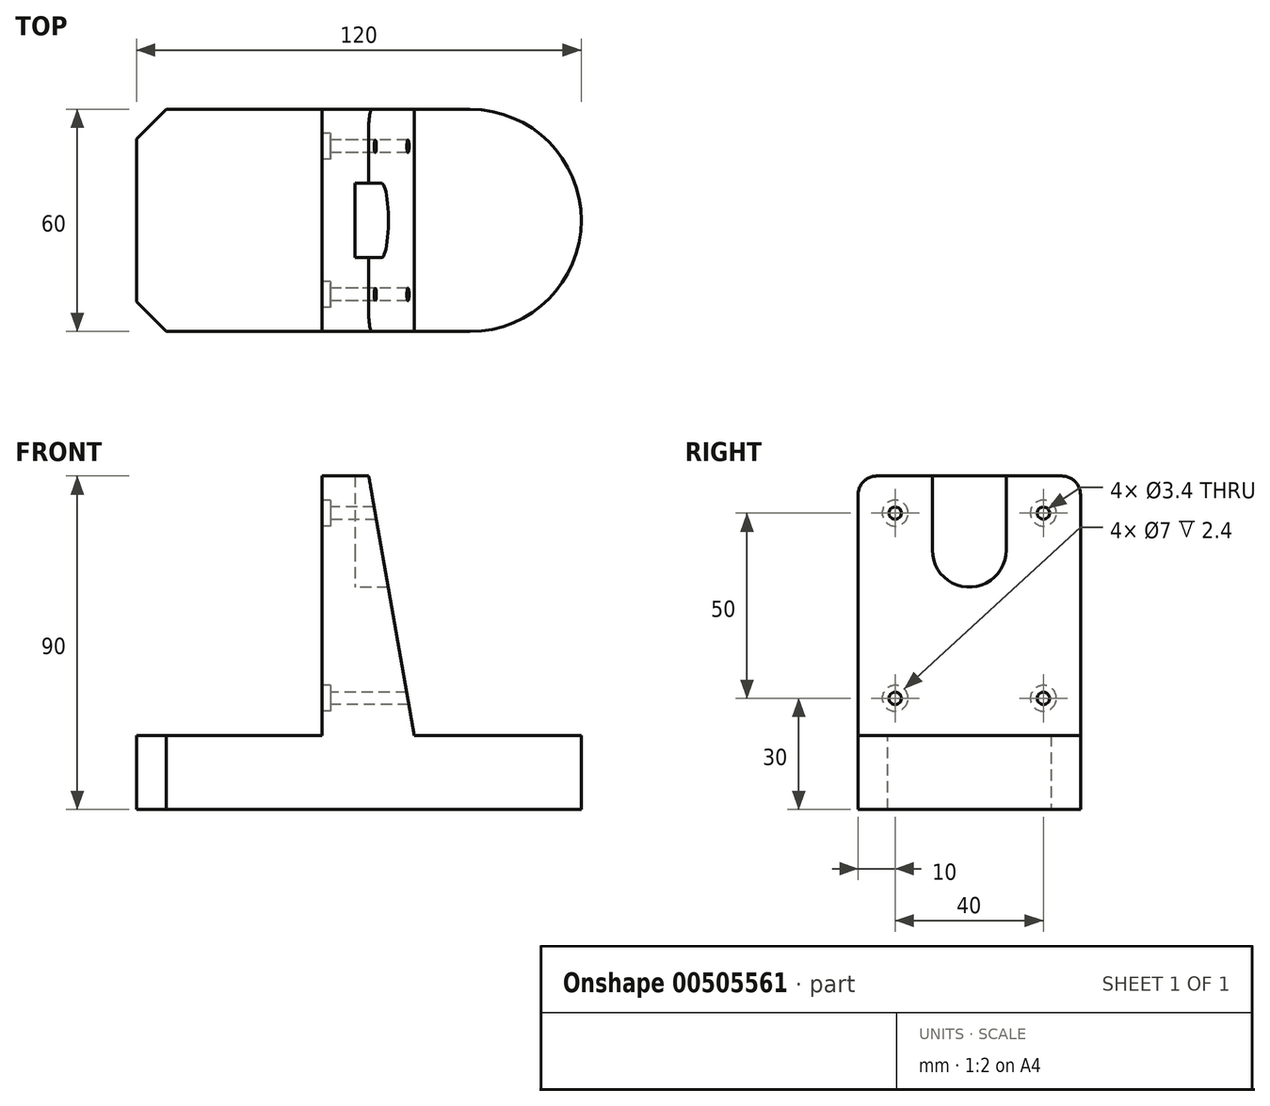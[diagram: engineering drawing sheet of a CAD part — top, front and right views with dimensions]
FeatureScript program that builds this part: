
annotation { "Feature Type Name" : "Feature", "Feature Type Description" : "" }
export const myFeature = defineFeature(function(context is Context, id is Id, definition is map)
    precondition{}
    {
        {
            var Q0;
            Q0=qCreatedBy(makeId("Top.planeOp"),FACE);
            var sketch = newSketch(context, id + "F0", { "sketchPlane" : qUnion([Q0])});
            skLineSegment(sketch, "E0.bottom", {"start": v(0, 0) * mm, "end": v(90, 0) * mm});
            skLineSegment(sketch, "E0.top", {"start": v(0, 60) * mm, "end": v(90, 60) * mm});
            skLineSegment(sketch, "E0.left", {"start": v(0, 0) * mm, "end": v(0, 60) * mm});
            skLineSegment(sketch, "E0.right", {"start": v(90, 0) * mm, "end": v(90, 60) * mm});
            skArc(sketch, "E1", {"start": v(90, 0) * mm, "mid": v(120, 30) * mm, "end": v(90, 60) * mm});
            skSolve(sketch);
        }
        {
            var Q0;
            Q0=qSketchRegion(id+"F0",true);
            extrude(context, id + "F1", {"entities" : qUnion([Q0]), "depth" : 20 * mm});
        }
        {
            var Q0;
            Q0=makeQuery(id+"F1.opExtrude","SWEPT_EDGE",EDGE,{"disambiguationData":[OSD([sQuery(id+"F0.wireOp",EDGE,"E0.bottom"),sQuery(id+"F0.wireOp",EDGE,"E0.left")])]});
            var Q1;
            Q1=makeQuery(id+"F1.opExtrude","SWEPT_EDGE",EDGE,{"disambiguationData":[OSD([sQuery(id+"F0.wireOp",EDGE,"E0.top"),sQuery(id+"F0.wireOp",EDGE,"E0.left")])]});
            chamfer(context, id + "F2", {"entities" : qUnion([Q0, Q1]), "width" : 8 * mm, "tangentPropagation" : true});
        }
        {
            var Q0;
            Q0=qCreatedBy(makeId("Front.planeOp"),FACE);
            var sketch = newSketch(context, id + "F3", { "sketchPlane" : qUnion([Q0])});
            skLineSegment(sketch, "E2", {"start": v(50, 20) * mm, "end": v(75, 20) * mm});
            skLineSegment(sketch, "E3", {"start": v(75, 20) * mm, "end": v(62.66, 90) * mm});
            skLineSegment(sketch, "E4", {"start": v(62.66, 90) * mm, "end": v(50, 90) * mm});
            skLineSegment(sketch, "E5", {"start": v(50, 90) * mm, "end": v(50, 20) * mm});
            skSolve(sketch);
        }
        {
            var Q0;
            Q0=qSketchRegion(id+"F3",true);
            var Q1;
            Q1=makeQuery(id+"F1.opExtrude","SWEPT_FACE",FACE,{"disambiguationData":[OSD([sQuery(id+"F0.wireOp",EDGE,"E0.top")])]});
            extrude(context, id + "F4", {"entities" : qUnion([Q0]), "operationType" : NewBodyOperationType.ADD, "endBound" : BoundingType.UP_TO_SURFACE, "oppositeDirection" : true, "endBoundEntityFace" : qUnion([Q1]), "depth" : 25 * mm});
        }
        {
            var Q0;
            Q0=makeQuery(id+"F4.opExtrude","CAP_EDGE",EDGE,{"disambiguationData":[OSD([sQuery(id+"F3.wireOp",EDGE,"E4")])],"isStart":true});
            var Q1;
            Q1=makeQuery(id+"F4.opExtrude","CAP_EDGE",EDGE,{"disambiguationData":[OSD([sQuery(id+"F3.wireOp",EDGE,"E4")])],"isStart":false});
            fillet(context, id + "F5", {"entities" : qUnion([Q0, Q1]), "radius" : 5 * mm, "tangentPropagation" : true, "allowEdgeOverflow" : false});
        }
        {
            var Q0;
            Q0=makeQuery(id+"F4.opExtrude","SWEPT_FACE",FACE,{"disambiguationData":[OSD([sQuery(id+"F3.wireOp",EDGE,"E5")])]});
            var sketch = newSketch(context, id + "F6", { "sketchPlane" : qUnion([Q0])});
            skLineSegment(sketch, "E6.bottom", {"start": v(-50, 30) * mm, "end": v(-10, 30) * mm, "construction": true});
            skLineSegment(sketch, "E6.top", {"start": v(-50, 80) * mm, "end": v(-10, 80) * mm, "construction": true});
            skLineSegment(sketch, "E6.left", {"start": v(-50, 30) * mm, "end": v(-50, 80) * mm, "construction": true});
            skLineSegment(sketch, "E6.right", {"start": v(-10, 30) * mm, "end": v(-10, 80) * mm, "construction": true});
            skPoint(sketch, "E7", {"position": v(-30, 80) * mm});
            skPoint(sketch, "E8", {"position": v(-30, 90) * mm});
            skSolve(sketch);
        }
        {
            var Q0;
            Q0=sQuery(id+"F6.wireOp",VERTEX,"E6.left.end");
            var Q1;
            Q1=sQuery(id+"F6.wireOp",VERTEX,"E6.left.start");
            var Q2;
            Q2=sQuery(id+"F6.wireOp",VERTEX,"E6.right.start");
            var Q3;
            Q3=sQuery(id+"F6.wireOp",VERTEX,"E6.right.end");
            var Q4;
            Q4=makeQuery(id+"F1.opExtrude","SWEPT_BODY",BODY,{"disambiguationData":[OSD([sQuery(id+"F0.wireOp",EDGE,"E0.bottom"),sQuery(id+"F0.wireOp",EDGE,"E0.top"),sQuery(id+"F0.wireOp",EDGE,"E0.left"),sQuery(id+"F0.wireOp",EDGE,"E1")])]});
            hole(context, id + "F7", {"style" : HoleStyle.C_BORE, "endStyle" : HoleEndStyle.THROUGH, "holeDiameter" : 3.4 * mm, "cBoreDiameter" : 7 * mm, "cBoreDepth" : 2.4 * mm, "isTappedThrough" : true, "tappedDepth" : 37.5 * mm, "tapClearance" : 3, "startFromSketch" : true, "locations" : qUnion([Q0, Q1, Q2, Q3]), "scope" : qUnion([Q4])});
        }
        {
            var Q0;
            Q0=makeQuery(id+"F4.opExtrude","SWEPT_FACE",FACE,{"disambiguationData":[OSD([sQuery(id+"F3.wireOp",EDGE,"E5")])]});
            cPlane(context, id + "F8", {"entities" : qUnion([Q0]), "cplaneType" : CPlaneType.OFFSET, "offset" : 9 * mm, "oppositeDirection" : true, "width" : 150 * mm, "height" : 150 * mm});
        }
        {
            var Q0;
            Q0=qCreatedBy(id+"F8.planeOp",FACE);
            var sketch = newSketch(context, id + "F9", { "sketchPlane" : qUnion([Q0])});
            skLineSegment(sketch, "E9.bottom", {"start": v(-20, 90) * mm, "end": v(-40, 90) * mm});
            skLineSegment(sketch, "E9.top", {"start": v(-20, 70) * mm, "end": v(-40, 70) * mm});
            skLineSegment(sketch, "E9.left", {"start": v(-20, 90) * mm, "end": v(-20, 70) * mm});
            skLineSegment(sketch, "E9.right", {"start": v(-40, 90) * mm, "end": v(-40, 70) * mm});
            skPoint(sketch, "E10", {"position": v(-30, 90) * mm});
            skArc(sketch, "E11", {"start": v(-40, 70) * mm, "mid": v(-30, 60) * mm, "end": v(-20, 70) * mm});
            skSolve(sketch);
        }
        {
            var Q0;
            Q0=qSketchRegion(id+"F9",true);
            extrude(context, id + "F10", {"entities" : qUnion([Q0]), "operationType" : NewBodyOperationType.REMOVE, "endBound" : BoundingType.UP_TO_NEXT, "oppositeDirection" : true, "depth" : 25 * mm});
        }
    });
